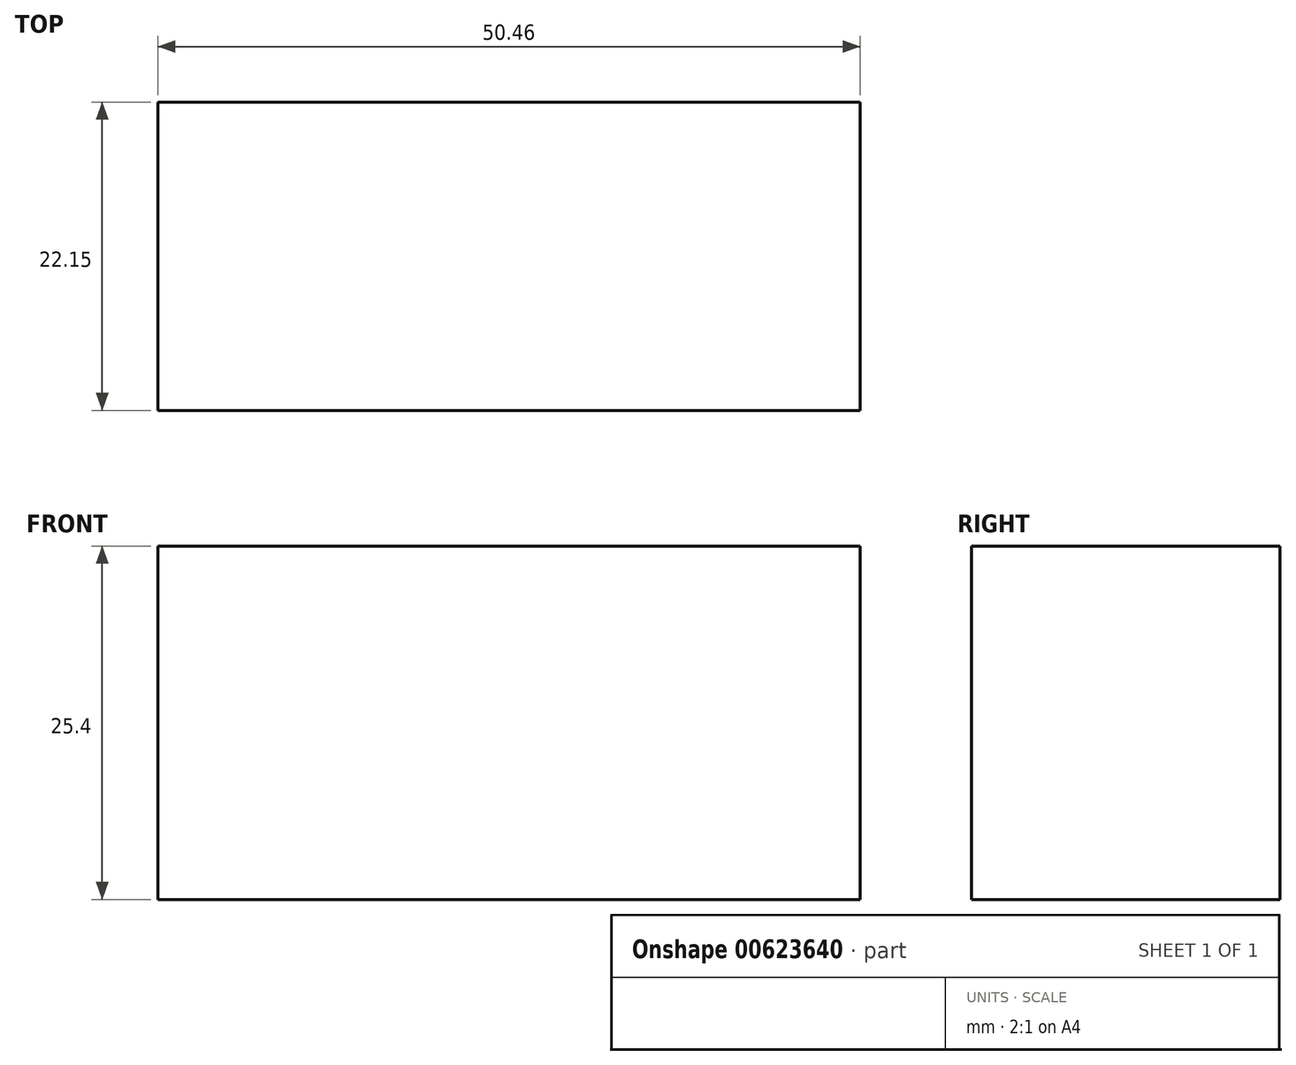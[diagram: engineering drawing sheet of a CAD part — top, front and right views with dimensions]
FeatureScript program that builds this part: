
annotation { "Feature Type Name" : "Feature", "Feature Type Description" : "" }
export const myFeature = defineFeature(function(context is Context, id is Id, definition is map)
    precondition{}
    {
        {
            var Q0;
            Q0=qCreatedBy(makeId("Top.planeOp"),FACE);
            var sketch = newSketch(context, id + "F0", { "sketchPlane" : qUnion([Q0])});
            skLineSegment(sketch, "E0", {"start": v(-26.23, 22.15) * mm, "end": v(24.23, 22.15) * mm});
            skLineSegment(sketch, "E1", {"start": v(24.23, 22.15) * mm, "end": v(24.23, 0) * mm});
            skLineSegment(sketch, "E2", {"start": v(24.23, 0) * mm, "end": v(-26.23, 0) * mm});
            skLineSegment(sketch, "E3", {"start": v(-26.23, 0) * mm, "end": v(-26.23, 22.15) * mm});
            skSolve(sketch);
        }
        {
            var Q0;
            Q0=makeQuery(id+"F0.imprint","IMPRINT",FACE,{"disambiguationData":[TD([[makeQuery(id+"F0.imprint","IMPRINT",EDGE,{"derivedFrom":sQuery(id+"F0.wireOp",EDGE,"E0")}),-1.0]])]});
            extrude(context, id + "F1", {"entities" : qUnion([Q0]), "depth" : 25.4 * mm, "offsetDistance" : 25.4 * mm});
        }
    });
